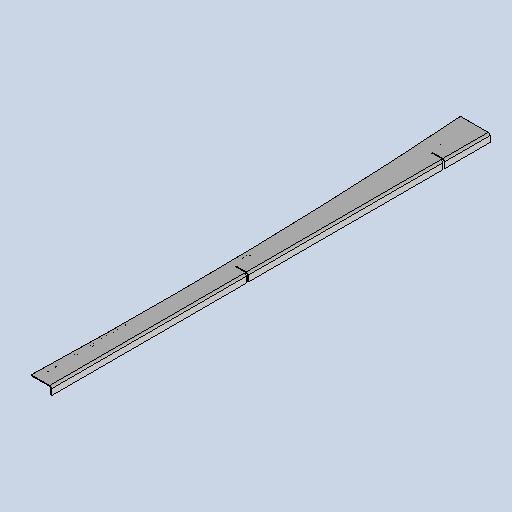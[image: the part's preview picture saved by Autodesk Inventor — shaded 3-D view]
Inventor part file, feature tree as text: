
AUTODESK INVENTOR PART (.ipt)
format: ipt  version: 2025 (Build 290162010, 162A)  size: 470,016 bytes
history: native  units: mm
features: sketch x6, other x5, sheet_metal_op x4, extrude x2, projected_geometry x2, chamfer x1, pattern_linear x1
ambient origin geometry x8: Origin, YZ Plane, XZ Plane, XY Plane, X Axis, Y Axis, Z Axis, Center Point
bodies: Body1 (feature_tree)
feature tree (21):
  sheet_metal_op  "Face2"
  sheet_metal_op  "Flange2"
  extrude  "Extrusion2"  Depth=6.0mm
  chamfer  "Chamfer2"  Distance=2.75mm
  pattern_linear  "Rectangular Pattern3"  Count1=2 Spacing1=90.0deg
  other  "Mark1"
  other  "A-Side Definition"
  extrude  "Extrusion3"  Depth=2.0mm
  sketch  "Sketch1"  dims[d16=1500.0mm d17=2700.0mm d18=2100.0mm d19=6.0mm d20=3.0mm d21=3.0mm d22=6.0mm d23=3.0mm d24=241.9mm d25=50.0mm d26=50.0mm d27=3.0mm d28=110.0mm d29=25.0mm d30=104.0mm d31=25.0mm d32=20.0mm d33=50.0mm d37=6.0mm d38=3.0mm d39=3.0mm]
  other  "Plate3"
  sketch  "Sketch3"  dims[d46=2.0mm]
  other  "Plate4"
  sheet_metal_op  "Bend2"
  sheet_metal_op  "Corner2"
  sketch  "Sketch5"  dims[d47=2.0mm]
  projected_geometry  "Projected Loop2"
  sketch  "Sketch Rectangular Pattern1"  dims[d43=3.0mm]
  sketch  "Sketch6"  dims[d48=1.0mm]
  sketch  "Sketch7"  dims[d49=4.0mm d50=2.75mm d51=20.0mm d52=90.0deg d53=2.75mm d54=8.0mm d55=2.0mm d56=2.75mm d57=500.0mm d58=500.0mm d59=500.0mm d60=500.0mm d61=500.0mm d69=1839.242466mm d70=2.0mm d71=0.0mm d72=0.0mm d76=67.563014mm d77=30.0mm d79=30.0mm d80=48.359031mm d81=30.0mm d83=250.0mm d84=40.0mm d86=550.0mm d87=10.0mm d89=10.0mm d91=274.556536mm d94=5.0mm d95=30.0mm d96=5.0mm d97=30.0mm d98=5.0mm d102=77.905549mm d104=51.799453mm d106=2.0mm d107=5.0mm d108=116.0mm d109=500.0mm d110=500.0mm d111=500.0mm d112=31.0mm d113=40.0mm d115=500.0mm d117=8.0mm d118=2.0mm d119=45.0deg d120=200.0mm d121=14.0mm d124=50.0mm d125=12.0mm d126=50.0mm d127=25.0mm d128=50.0mm d129=12.0mm d130=50.0mm d131=12.0mm d132=50.0mm d133=12.0mm d134=50.0mm d135=25.0mm d136=25.0mm d137=25.0mm d138=50.0mm d139=50.0mm d140=50.0mm d141=0.0mm d142=0.0mm d143=100.0mm]
  projected_geometry  "Projected Loop3"
  other  "Definition1"
